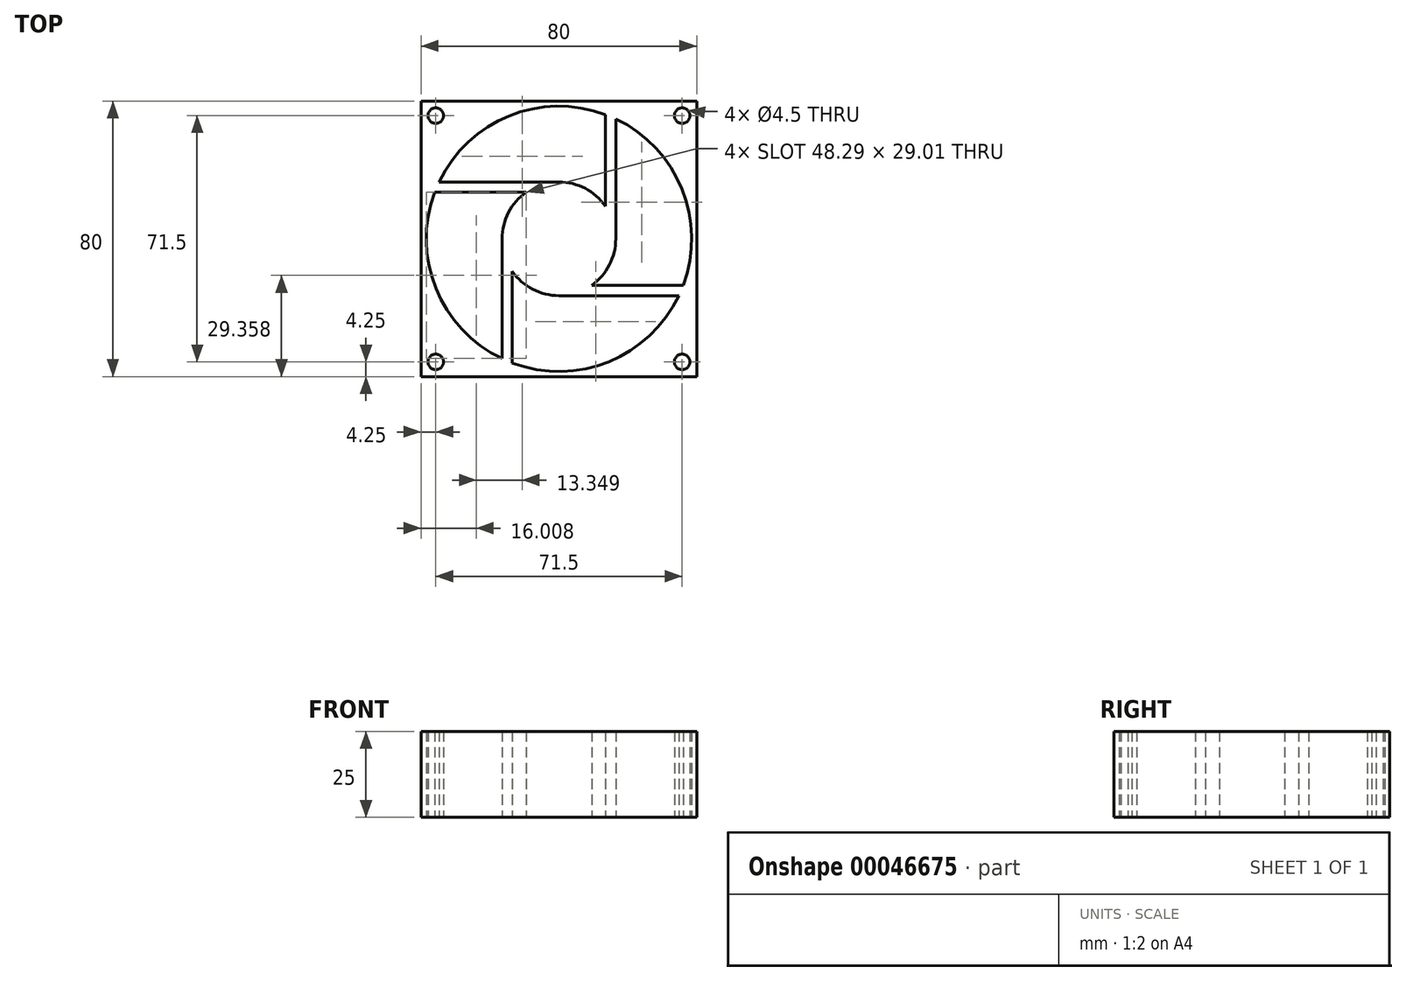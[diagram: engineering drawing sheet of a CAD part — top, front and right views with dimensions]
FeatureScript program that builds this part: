
annotation { "Feature Type Name" : "Feature", "Feature Type Description" : "" }
export const myFeature = defineFeature(function(context is Context, id is Id, definition is map)
    precondition{}
    {
        {
            var Q0;
            Q0=qCreatedBy(makeId("Top.planeOp"),FACE);
            var sketch = newSketch(context, id + "F0", { "sketchPlane" : qUnion([Q0])});
            skLineSegment(sketch, "E0.bottom", {"start": v(-40, 40) * mm, "end": v(40, 40) * mm});
            skLineSegment(sketch, "E0.top", {"start": v(-40, -40) * mm, "end": v(40, -40) * mm});
            skLineSegment(sketch, "E0.left", {"start": v(-40, 40) * mm, "end": v(-40, -40) * mm});
            skLineSegment(sketch, "E0.right", {"start": v(40, 40) * mm, "end": v(40, -40) * mm});
            skLineSegment(sketch, "E1", {"start": v(-40, 40) * mm, "end": v(40, -40) * mm, "construction": true});
            skCircle(sketch, "E2", {"center": v(0, 0) * mm, "radius": 38.5 * mm});
            skLineSegment(sketch, "E3", {"start": v(-40, -40) * mm, "end": v(40, 40) * mm, "construction": true});
            skLineSegment(sketch, "E4.bottom", {"start": v(-35.75, 35.75) * mm, "end": v(35.75, 35.75) * mm, "construction": true});
            skLineSegment(sketch, "E4.top", {"start": v(-35.75, -35.75) * mm, "end": v(35.75, -35.75) * mm, "construction": true});
            skLineSegment(sketch, "E4.left", {"start": v(-35.75, 35.75) * mm, "end": v(-35.75, -35.75) * mm, "construction": true});
            skLineSegment(sketch, "E4.right", {"start": v(35.75, 35.75) * mm, "end": v(35.75, -35.75) * mm, "construction": true});
            skCircle(sketch, "E5", {"center": v(35.75, 35.75) * mm, "radius": 2.25 * mm});
            skCircle(sketch, "E6", {"center": v(-35.75, 35.75) * mm, "radius": 2.25 * mm});
            skCircle(sketch, "E7", {"center": v(-35.75, -35.75) * mm, "radius": 2.25 * mm});
            skCircle(sketch, "E8", {"center": v(35.75, -35.75) * mm, "radius": 2.25 * mm});
            skSolve(sketch);
        }
        {
            var Q0;
            Q0 = qSketchRegion(id + "F0", true);
            extrude(context, id + "F1", {"entities" : qUnion([Q0]), "depth" : 25 * mm});
        }
        {
            var Q0;
            Q0=qCreatedBy(makeId("Top.planeOp"),FACE);
            var sketch = newSketch(context, id + "F2", { "sketchPlane" : qUnion([Q0])});
            skCircle(sketch, "E9", {"center": v(0, 0) * mm, "radius": 16.5 * mm});
            skLineSegment(sketch, "E10.bottom", {"start": v(0, 13.5) * mm, "end": v(-36.06, 13.5) * mm});
            skLineSegment(sketch, "E10.top", {"start": v(0, 16.5) * mm, "end": v(-36.06, 16.5) * mm});
            skLineSegment(sketch, "E10.left", {"start": v(0, 13.5) * mm, "end": v(0, 16.5) * mm});
            skLineSegment(sketch, "E10.right", {"start": v(-36.06, 13.5) * mm, "end": v(-36.06, 16.5) * mm});
            skCircle(sketch, "E11.0", {"center": v(0, 0) * mm, "radius": 38.5 * mm});
            skLineSegment(sketch, "E12.1.0", {"start": v(-16.5, 0) * mm, "end": v(-16.5, -36.06) * mm});
            skLineSegment(sketch, "E12.1.1", {"start": v(-13.5, 0) * mm, "end": v(-13.5, -36.06) * mm});
            skLineSegment(sketch, "E12.1.2", {"start": v(-13.5, 0) * mm, "end": v(-16.5, 0) * mm});
            skLineSegment(sketch, "E12.1.3", {"start": v(-13.5, -36.06) * mm, "end": v(-16.5, -36.06) * mm});
            skLineSegment(sketch, "E12.2.0", {"start": v(0, -16.5) * mm, "end": v(36.06, -16.5) * mm});
            skLineSegment(sketch, "E12.2.1", {"start": v(0, -13.5) * mm, "end": v(36.06, -13.5) * mm});
            skLineSegment(sketch, "E12.2.2", {"start": v(0, -13.5) * mm, "end": v(0, -16.5) * mm});
            skLineSegment(sketch, "E12.2.3", {"start": v(36.06, -13.5) * mm, "end": v(36.06, -16.5) * mm});
            skLineSegment(sketch, "E12.3.0", {"start": v(16.5, 0) * mm, "end": v(16.5, 36.06) * mm});
            skLineSegment(sketch, "E12.3.1", {"start": v(13.5, 0) * mm, "end": v(13.5, 36.06) * mm});
            skLineSegment(sketch, "E12.3.2", {"start": v(13.5, 0) * mm, "end": v(16.5, 0) * mm});
            skLineSegment(sketch, "E12.3.3", {"start": v(13.5, 36.06) * mm, "end": v(16.5, 36.06) * mm});
            skSolve(sketch);
        }
        {
            var Q0;
            {var subQ12=sQuery(id+"F2.wireOp",EDGE,"E10.left");Q0=makeQuery(id+"F2.imprint","IMPRINT",FACE,{"disambiguationData":[TD([[makeQuery(id+"F2.imprint","IMPRINT",EDGE,{"derivedFrom":subQ12}),-1.0]])]});}
            var Q1;
            {var subQ0=sQuery(id+"F2.wireOp",EDGE,"E12.3.1");var subQ1=sQuery(id+"F2.wireOp",EDGE,"E9");var subQ2=makeQuery(id+"F2.imprint","INTERSECT",VERTEX,{"derivedFrom":[subQ1,subQ0]});Q1=makeQuery(id+"F2.imprint","IMPRINT",FACE,{"disambiguationData":[TD([[makeQuery(id+"F2.imprint","IMPRINT",EDGE,{"disambiguationData":[TD([[subQ2,1.0]])],"derivedFrom":subQ1}),-1.0]])]});}
            var Q2;
            {var subQ0=sQuery(id+"F2.wireOp",EDGE,"E12.3.2");Q2=makeQuery(id+"F2.imprint","IMPRINT",FACE,{"disambiguationData":[TD([[makeQuery(id+"F2.imprint","IMPRINT",EDGE,{"derivedFrom":subQ0}),1.0]])]});}
            var Q3;
            {var subQ0=sQuery(id+"F2.wireOp",EDGE,"E10.left");Q3=makeQuery(id+"F2.imprint","IMPRINT",FACE,{"disambiguationData":[TD([[makeQuery(id+"F2.imprint","IMPRINT",EDGE,{"derivedFrom":subQ0}),1.0]])]});}
            var Q4;
            {var subQ3=sQuery(id+"F2.wireOp",EDGE,"E10.bottom");var subQ5=sQuery(id+"F2.wireOp",EDGE,"E9");var subQ7=makeQuery(id+"F2.imprint","INTERSECT",VERTEX,{"derivedFrom":[subQ5,subQ3]});Q4=makeQuery(id+"F2.imprint","IMPRINT",FACE,{"disambiguationData":[TD([[makeQuery(id+"F2.imprint","IMPRINT",EDGE,{"disambiguationData":[TD([[subQ7,1.0]])],"derivedFrom":subQ5}),-1.0]])]});}
            var Q5;
            {var subQ0=sQuery(id+"F2.wireOp",EDGE,"E12.1.2");Q5=makeQuery(id+"F2.imprint","IMPRINT",FACE,{"disambiguationData":[TD([[makeQuery(id+"F2.imprint","IMPRINT",EDGE,{"derivedFrom":subQ0}),1.0]])]});}
            var Q6;
            {var subQ0=sQuery(id+"F2.wireOp",EDGE,"E12.1.1");var subQ1=sQuery(id+"F2.wireOp",EDGE,"E9");var subQ2=makeQuery(id+"F2.imprint","INTERSECT",VERTEX,{"derivedFrom":[subQ1,subQ0]});Q6=makeQuery(id+"F2.imprint","IMPRINT",FACE,{"disambiguationData":[TD([[makeQuery(id+"F2.imprint","IMPRINT",EDGE,{"disambiguationData":[TD([[subQ2,1.0]])],"derivedFrom":subQ1}),-1.0]])]});}
            var Q7;
            {var subQ0=sQuery(id+"F2.wireOp",EDGE,"E12.2.2");Q7=makeQuery(id+"F2.imprint","IMPRINT",FACE,{"disambiguationData":[TD([[makeQuery(id+"F2.imprint","IMPRINT",EDGE,{"derivedFrom":subQ0}),1.0]])]});}
            var Q8;
            {var subQ0=sQuery(id+"F2.wireOp",EDGE,"E12.2.1");var subQ1=sQuery(id+"F2.wireOp",EDGE,"E9");var subQ2=makeQuery(id+"F2.imprint","INTERSECT",VERTEX,{"derivedFrom":[subQ1,subQ0]});Q8=makeQuery(id+"F2.imprint","IMPRINT",FACE,{"disambiguationData":[TD([[makeQuery(id+"F2.imprint","IMPRINT",EDGE,{"disambiguationData":[TD([[subQ2,1.0]])],"derivedFrom":subQ1}),-1.0]])]});}
            extrude(context, id + "F3", {"entities" : qUnion([Q0, Q1, Q2, Q3, Q4, Q5, Q6, Q7, Q8]), "operationType" : NewBodyOperationType.ADD, "depth" : 25 * mm});
        }
    });
